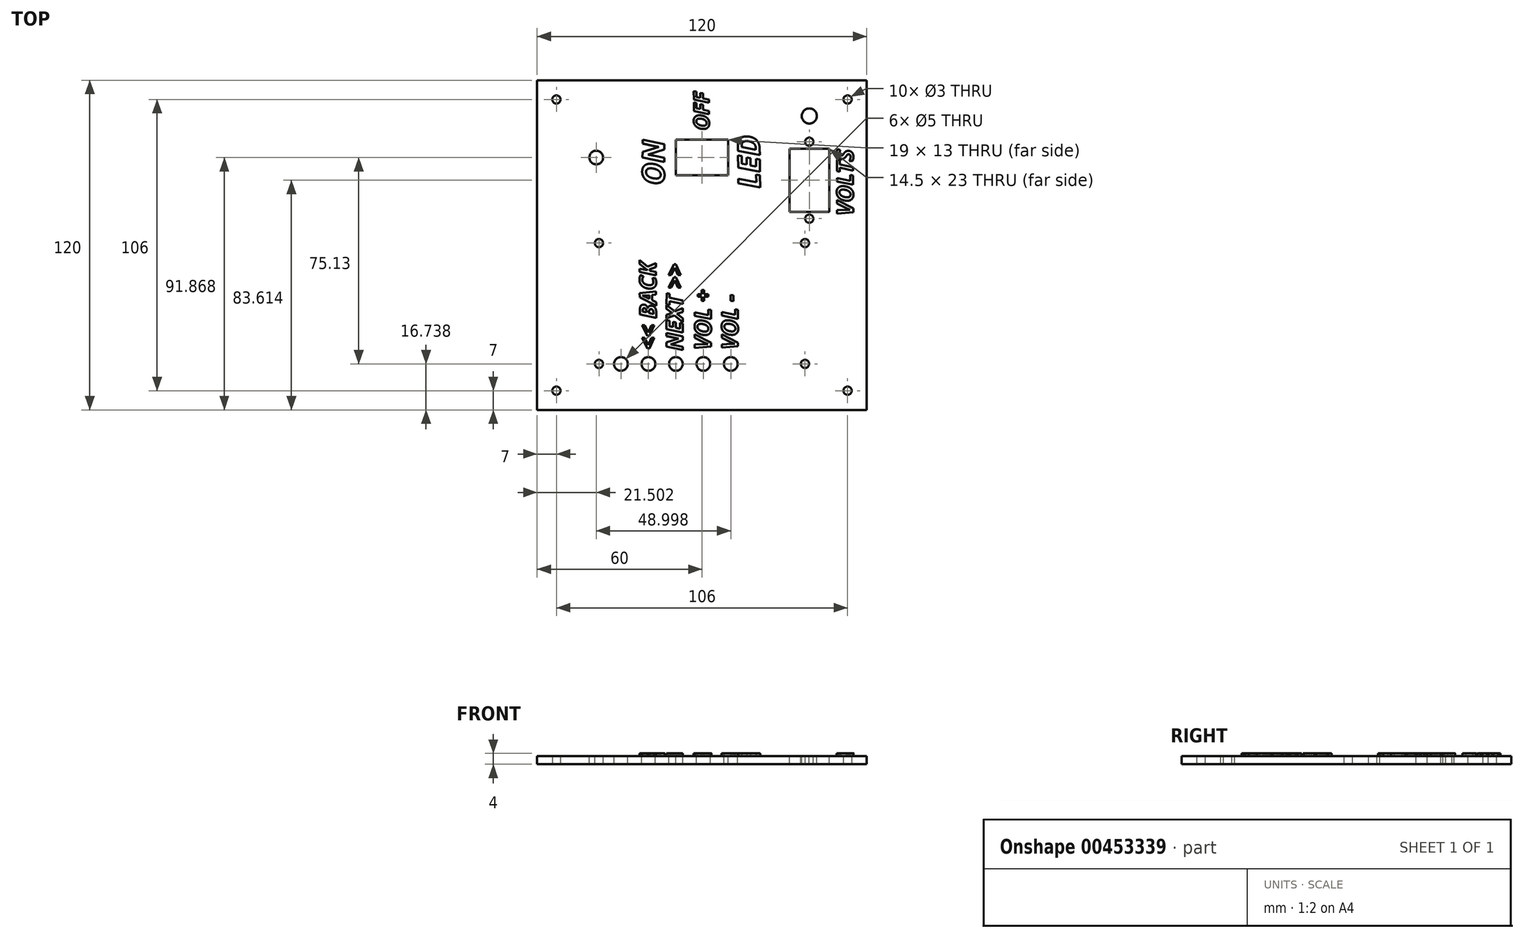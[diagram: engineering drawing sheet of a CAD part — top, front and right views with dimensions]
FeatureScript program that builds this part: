
annotation { "Feature Type Name" : "Feature", "Feature Type Description" : "" }
export const myFeature = defineFeature(function(context is Context, id is Id, definition is map)
    precondition{}
    {
        {
            var Q0;
            Q0=qCreatedBy(makeId("Top.planeOp"),FACE);
            var sketch = newSketch(context, id + "F0", { "sketchPlane" : qUnion([Q0])});
            skLineSegment(sketch, "E0.bottom", {"start": v(60, 60) * mm, "end": v(-60, 60) * mm});
            skLineSegment(sketch, "E0.top", {"start": v(60, -60) * mm, "end": v(-60, -60) * mm});
            skLineSegment(sketch, "E0.left", {"start": v(60, 60) * mm, "end": v(60, -60) * mm});
            skLineSegment(sketch, "E0.right", {"start": v(-60, 60) * mm, "end": v(-60, -60) * mm});
            skPoint(sketch, "E0.middle", {"position": v(0, 0) * mm});
            skLineSegment(sketch, "E1.0", {"start": v(-53, 53) * mm, "end": v(-53, -53) * mm, "construction": true});
            skLineSegment(sketch, "E1.1", {"start": v(53, 53) * mm, "end": v(-53, 53) * mm, "construction": true});
            skLineSegment(sketch, "E1.2", {"start": v(53, 53) * mm, "end": v(53, -53) * mm, "construction": true});
            skLineSegment(sketch, "E1.3", {"start": v(53, -53) * mm, "end": v(-53, -53) * mm, "construction": true});
            skCircle(sketch, "E2", {"center": v(-53, -53) * mm, "radius": 1.5 * mm});
            skCircle(sketch, "E3", {"center": v(-53, 53) * mm, "radius": 1.5 * mm});
            skCircle(sketch, "E4", {"center": v(53, 53) * mm, "radius": 1.5 * mm});
            skCircle(sketch, "E5", {"center": v(53, -53) * mm, "radius": 1.5 * mm});
            skSolve(sketch);
        }
        {
            var Q0;
            Q0 = qSketchRegion(id + "F0", true);
            extrude(context, id + "F1", {"entities" : qUnion([Q0]), "depth" : 3 * mm});
        }
        {
            var Q0;
            Q0=makeQuery(id+"F1.opExtrude","CAP_FACE",FACE,{"disambiguationData":[OSD([sQuery(id+"F0.wireOp",EDGE,"E0.bottom"),sQuery(id+"F0.wireOp",EDGE,"E0.top"),sQuery(id+"F0.wireOp",EDGE,"E0.left"),sQuery(id+"F0.wireOp",EDGE,"E0.right")])],"isStart":false});
            var sketch = newSketch(context, id + "F2", { "sketchPlane" : qUnion([Q0])});
            skLineSegment(sketch, "E6.bottom", {"start": v(37.5, 0.74) * mm, "end": v(-37.5, 0.74) * mm, "construction": true});
            skLineSegment(sketch, "E6.top", {"start": v(37.5, -43.26) * mm, "end": v(-37.5, -43.26) * mm, "construction": true});
            skLineSegment(sketch, "E6.left", {"start": v(37.5, 0.74) * mm, "end": v(37.5, -43.26) * mm, "construction": true});
            skLineSegment(sketch, "E6.right", {"start": v(-37.5, 0.74) * mm, "end": v(-37.5, -43.26) * mm, "construction": true});
            skPoint(sketch, "E6.middle", {"position": v(0, -21.26) * mm});
            skCircle(sketch, "E7", {"center": v(-37.5, 0.74) * mm, "radius": 1.5 * mm});
            skCircle(sketch, "E8", {"center": v(37.5, 0.74) * mm, "radius": 1.5 * mm});
            skCircle(sketch, "E9", {"center": v(37.5, -43.26) * mm, "radius": 1.5 * mm});
            skCircle(sketch, "E10", {"center": v(-37.5, -43.26) * mm, "radius": 1.5 * mm});
            skCircle(sketch, "E11", {"center": v(-29.5, -43.26) * mm, "radius": 2.5 * mm});
            skCircle(sketch, "E12", {"center": v(-19.5, -43.26) * mm, "radius": 2.5 * mm});
            skCircle(sketch, "E13", {"center": v(-9.5, -43.26) * mm, "radius": 2.5 * mm});
            skCircle(sketch, "E14", {"center": v(0.5, -43.26) * mm, "radius": 2.5 * mm});
            skCircle(sketch, "E15", {"center": v(10.5, -43.26) * mm, "radius": 2.5 * mm});
            skLineSegment(sketch, "E16.bottom", {"start": v(9.5, 38.37) * mm, "end": v(-9.5, 38.37) * mm});
            skLineSegment(sketch, "E16.top", {"start": v(9.5, 25.37) * mm, "end": v(-9.5, 25.37) * mm});
            skLineSegment(sketch, "E16.left", {"start": v(9.5, 38.37) * mm, "end": v(9.5, 25.37) * mm});
            skLineSegment(sketch, "E16.right", {"start": v(-9.5, 38.37) * mm, "end": v(-9.5, 25.37) * mm});
            skPoint(sketch, "E16.middle", {"position": v(0, 31.87) * mm});
            skSolve(sketch);
        }
        {
            var Q0;
            Q0=makeQuery(id+"F2.imprint","IMPRINT",FACE,{"disambiguationData":[TD([[makeQuery(id+"F2.imprint","IMPRINT",EDGE,{"derivedFrom":sQuery(id+"F2.wireOp",EDGE,"E7")}),-1.0]])]});
            var sketch = newSketch(context, id + "F3", { "sketchPlane" : qUnion([Q0])});
            skText(sketch, "E17", { "text": "PLAY", "fontName": "OpenSans-BoldItalic.ttf"});
            const initialGuessF3  = {"E17": [-0.02621, -0.03806, -0.00037, 1, 0.006]};
            skSetInitialGuess(sketch, initialGuessF3);
            skSolve(sketch);
        }
        {
            var Q0;
            Q0 = qConstructionFilter(qBodyType(qCreatedBy(id + "F3" ,EDGE), BodyType.WIRE), ConstructionObject.NO);
            extrude(context, id + "F4", {"bodyType" : ToolBodyType.SURFACE, "surfaceEntities" : qUnion([Q0]), "depth" : 1 * mm});
        }
        {
            var Q0;
            Q0=makeQuery(id+"F2.imprint","IMPRINT",FACE,{"disambiguationData":[TD([[makeQuery(id+"F2.imprint","IMPRINT",EDGE,{"derivedFrom":sQuery(id+"F2.wireOp",EDGE,"E7")}),-1.0]])]});
            var sketch = newSketch(context, id + "F5", { "sketchPlane" : qUnion([Q0])});
            skText(sketch, "E18", { "text": "<< BACK", "fontName": "OpenSans-BoldItalic.ttf"});
            const initialGuessF5  = {"E18": [-0.01657, -0.03808, -0.00626, 0.99998, 0.006]};
            skSetInitialGuess(sketch, initialGuessF5);
            skSolve(sketch);
        }
        {
            var Q0;
            Q0 = qSketchRegion(id + "F5", true);
            extrude(context, id + "F6", {"entities" : qUnion([Q0]), "operationType" : NewBodyOperationType.ADD, "depth" : 1 * mm});
        }
        {
            var Q0;
            Q0=makeQuery(id+"F2.imprint","IMPRINT",FACE,{"disambiguationData":[TD([[makeQuery(id+"F2.imprint","IMPRINT",EDGE,{"derivedFrom":sQuery(id+"F2.wireOp",EDGE,"E7")}),-1.0]])]});
            var sketch = newSketch(context, id + "F7", { "sketchPlane" : qUnion([Q0])});
            skText(sketch, "E19", { "text": "NEXT >>", "fontName": "OpenSans-BoldItalic.ttf"});
            const initialGuessF7  = {"E19": [-0.00696, -0.03837, 0.00128, 1, 0.006]};
            skSetInitialGuess(sketch, initialGuessF7);
            skSolve(sketch);
        }
        {
            var Q0;
            Q0 = qSketchRegion(id + "F7", true);
            extrude(context, id + "F8", {"entities" : qUnion([Q0]), "operationType" : NewBodyOperationType.ADD, "depth" : 1 * mm});
        }
        {
            var Q0;
            Q0=makeQuery(id+"F2.imprint","IMPRINT",FACE,{"disambiguationData":[TD([[makeQuery(id+"F2.imprint","IMPRINT",EDGE,{"derivedFrom":sQuery(id+"F2.wireOp",EDGE,"E7")}),-1.0]])]});
            var sketch = newSketch(context, id + "F9", { "sketchPlane" : qUnion([Q0])});
            skText(sketch, "E20", { "text": "VOL +", "fontName": "OpenSans-BoldItalic.ttf"});
            const initialGuessF9  = {"E20": [0.00332, -0.03817, -0.00012, 1, 0.006]};
            skSetInitialGuess(sketch, initialGuessF9);
            skSolve(sketch);
        }
        {
            var Q0;
            Q0 = qSketchRegion(id + "F9", true);
            extrude(context, id + "F10", {"entities" : qUnion([Q0]), "operationType" : NewBodyOperationType.ADD, "depth" : 1 * mm});
        }
        {
            var Q0;
            Q0=makeQuery(id+"F2.imprint","IMPRINT",FACE,{"disambiguationData":[TD([[makeQuery(id+"F2.imprint","IMPRINT",EDGE,{"derivedFrom":sQuery(id+"F2.wireOp",EDGE,"E7")}),-1.0]])]});
            var sketch = newSketch(context, id + "F11", { "sketchPlane" : qUnion([Q0])});
            skText(sketch, "E21", { "text": "VOL -", "fontName": "OpenSans-BoldItalic.ttf"});
            const initialGuessF11  = {"E21": [0.01313, -0.03811, 0.00122, 1, 0.006]};
            skSetInitialGuess(sketch, initialGuessF11);
            skSolve(sketch);
        }
        {
            var Q0;
            Q0 = qSketchRegion(id + "F11", true);
            extrude(context, id + "F12", {"entities" : qUnion([Q0]), "operationType" : NewBodyOperationType.ADD, "depth" : 1 * mm});
        }
        {
            var Q0;
            Q0 = qSketchRegion(id + "F0", true);
            extrude(context, id + "F13", {"entities" : qUnion([Q0]), "operationType" : NewBodyOperationType.REMOVE, "oppositeDirection" : true, "depth" : 4 * mm});
        }
        {
            var Q0;
            Q0 = qSketchRegion(id + "F2", true);
            extrude(context, id + "F14", {"entities" : qUnion([Q0]), "operationType" : NewBodyOperationType.REMOVE, "oppositeDirection" : true, "depth" : 3 * mm});
        }
        {
            var Q0;
            {var subQ92=sQuery(id+"F0.wireOp",EDGE,"E0.right");var subQ95=sQuery(id+"F0.wireOp",EDGE,"E3");var subQ98=sQuery(id+"F0.wireOp",EDGE,"E4");var subQ103=sQuery(id+"F0.wireOp",EDGE,"E0.left");var subQ105=sQuery(id+"F0.wireOp",EDGE,"E5");var subQ107=sQuery(id+"F0.wireOp",EDGE,"E0.top");var subQ110=sQuery(id+"F0.wireOp",EDGE,"E2");var subQ132=sQuery(id+"F0.wireOp",EDGE,"E0.bottom");var subQ133=makeQuery(id+"F1.opExtrude","SWEPT_FACE",FACE,{"disambiguationData":[OSD([subQ132])]});Q0=makeQuery(id+"F12.boolean.opBoolean","SPLIT",FACE,{"disambiguationData":[TD([subQ133])],"derivedFrom":makeQuery(id+"F10.boolean.opBoolean","SPLIT",FACE,{"disambiguationData":[TD([subQ133])],"derivedFrom":makeQuery(id+"F6.boolean.opBoolean","SPLIT",FACE,{"disambiguationData":[TD([subQ133])],"derivedFrom":makeQuery(id+"F1.opExtrude","CAP_FACE",FACE,{"disambiguationData":[OSD([subQ132,subQ107,subQ103,subQ92,subQ110,subQ95,subQ98,subQ105])],"isStart":false})})})});}
            var sketch = newSketch(context, id + "F15", { "sketchPlane" : qUnion([Q0])});
            skText(sketch, "E22", { "text": "ON", "fontName": "OpenSans-BoldItalic.ttf"});
            const initialGuessF15  = {"E22": [-0.01374, 0.02185, 0.0028, 1, 0.008]};
            skSetInitialGuess(sketch, initialGuessF15);
            skSolve(sketch);
        }
        {
            var Q0;
            Q0 = qSketchRegion(id + "F15", true);
            extrude(context, id + "F16", {"entities" : qUnion([Q0]), "operationType" : NewBodyOperationType.ADD, "depth" : 1 * mm});
        }
        {
            var Q0;
            {var subQ66=sQuery(id+"F0.wireOp",EDGE,"E0.bottom");var subQ67=makeQuery(id+"F1.opExtrude","SWEPT_FACE",FACE,{"disambiguationData":[OSD([subQ66])]});var subQ88=sQuery(id+"F0.wireOp",EDGE,"E2");var subQ90=sQuery(id+"F0.wireOp",EDGE,"E0.top");var subQ92=sQuery(id+"F0.wireOp",EDGE,"E5");var subQ94=sQuery(id+"F0.wireOp",EDGE,"E0.left");var subQ99=sQuery(id+"F0.wireOp",EDGE,"E4");var subQ102=sQuery(id+"F0.wireOp",EDGE,"E3");var subQ105=sQuery(id+"F0.wireOp",EDGE,"E0.right");Q0=makeQuery(id+"F16.boolean.opBoolean","SPLIT",FACE,{"disambiguationData":[TD([subQ67])],"derivedFrom":makeQuery(id+"F12.boolean.opBoolean","SPLIT",FACE,{"disambiguationData":[TD([subQ67])],"derivedFrom":makeQuery(id+"F10.boolean.opBoolean","SPLIT",FACE,{"disambiguationData":[TD([subQ67])],"derivedFrom":makeQuery(id+"F6.boolean.opBoolean","SPLIT",FACE,{"disambiguationData":[TD([subQ67])],"derivedFrom":makeQuery(id+"F1.opExtrude","CAP_FACE",FACE,{"disambiguationData":[OSD([subQ66,subQ90,subQ94,subQ105,subQ88,subQ102,subQ99,subQ92])],"isStart":false})})})})});}
            var sketch = newSketch(context, id + "F17", { "sketchPlane" : qUnion([Q0])});
            skText(sketch, "E23", { "text": "LED", "fontName": "OpenSans-BoldItalic.ttf"});
            const initialGuessF17  = {"E23": [0.02119, 0.02066, -0.01332, 0.99991, 0.008]};
            skSetInitialGuess(sketch, initialGuessF17);
            skSolve(sketch);
        }
        {
            var Q0;
            Q0 = qSketchRegion(id + "F17", true);
            extrude(context, id + "F18", {"entities" : qUnion([Q0]), "operationType" : NewBodyOperationType.ADD, "depth" : 1 * mm});
        }
        {
            var Q0;
            Q0 = qSketchRegion(id + "F2", true);
            extrude(context, id + "F19", {"entities" : qUnion([Q0]), "operationType" : NewBodyOperationType.REMOVE, "oppositeDirection" : true, "depth" : 5 * mm});
        }
        {
            var Q0;
            {var subQ78=sQuery(id+"F0.wireOp",EDGE,"E0.bottom");var subQ79=makeQuery(id+"F1.opExtrude","SWEPT_FACE",FACE,{"disambiguationData":[OSD([subQ78])]});var subQ100=sQuery(id+"F0.wireOp",EDGE,"E2");var subQ102=sQuery(id+"F0.wireOp",EDGE,"E0.top");var subQ104=sQuery(id+"F0.wireOp",EDGE,"E5");var subQ106=sQuery(id+"F0.wireOp",EDGE,"E0.left");var subQ111=sQuery(id+"F0.wireOp",EDGE,"E4");var subQ114=sQuery(id+"F0.wireOp",EDGE,"E3");var subQ117=sQuery(id+"F0.wireOp",EDGE,"E0.right");Q0=makeQuery(id+"F18.boolean.opBoolean","SPLIT",FACE,{"disambiguationData":[TD([subQ79])],"derivedFrom":makeQuery(id+"F16.boolean.opBoolean","SPLIT",FACE,{"disambiguationData":[TD([subQ79])],"derivedFrom":makeQuery(id+"F12.boolean.opBoolean","SPLIT",FACE,{"disambiguationData":[TD([subQ79])],"derivedFrom":makeQuery(id+"F10.boolean.opBoolean","SPLIT",FACE,{"disambiguationData":[TD([subQ79])],"derivedFrom":makeQuery(id+"F6.boolean.opBoolean","SPLIT",FACE,{"disambiguationData":[TD([subQ79])],"derivedFrom":makeQuery(id+"F1.opExtrude","CAP_FACE",FACE,{"disambiguationData":[OSD([subQ78,subQ102,subQ106,subQ117,subQ100,subQ114,subQ111,subQ104])],"isStart":false})})})})})});}
            var sketch = newSketch(context, id + "F20", { "sketchPlane" : qUnion([Q0])});
            skText(sketch, "E24", { "text": "OFF", "fontName": "OpenSans-BoldItalic.ttf"});
            const initialGuessF20  = {"E24": [0.0026, 0.0418, -0.00228, 1, 0.0056]};
            skSetInitialGuess(sketch, initialGuessF20);
            skSolve(sketch);
        }
        {
            var Q0;
            Q0 = qSketchRegion(id + "F20", true);
            extrude(context, id + "F21", {"entities" : qUnion([Q0]), "operationType" : NewBodyOperationType.ADD, "depth" : 1 * mm});
        }
        {
            var Q0;
            {var subQ83=sQuery(id+"F0.wireOp",EDGE,"E0.bottom");var subQ84=makeQuery(id+"F1.opExtrude","SWEPT_FACE",FACE,{"disambiguationData":[OSD([subQ83])]});var subQ105=sQuery(id+"F0.wireOp",EDGE,"E2");var subQ107=sQuery(id+"F0.wireOp",EDGE,"E0.top");var subQ109=sQuery(id+"F0.wireOp",EDGE,"E5");var subQ111=sQuery(id+"F0.wireOp",EDGE,"E0.left");var subQ116=sQuery(id+"F0.wireOp",EDGE,"E4");var subQ119=sQuery(id+"F0.wireOp",EDGE,"E3");var subQ122=sQuery(id+"F0.wireOp",EDGE,"E0.right");Q0=makeQuery(id+"F21.boolean.opBoolean","SPLIT",FACE,{"disambiguationData":[TD([subQ84])],"derivedFrom":makeQuery(id+"F18.boolean.opBoolean","SPLIT",FACE,{"disambiguationData":[TD([subQ84])],"derivedFrom":makeQuery(id+"F16.boolean.opBoolean","SPLIT",FACE,{"disambiguationData":[TD([subQ84])],"derivedFrom":makeQuery(id+"F12.boolean.opBoolean","SPLIT",FACE,{"disambiguationData":[TD([subQ84])],"derivedFrom":makeQuery(id+"F10.boolean.opBoolean","SPLIT",FACE,{"disambiguationData":[TD([subQ84])],"derivedFrom":makeQuery(id+"F6.boolean.opBoolean","SPLIT",FACE,{"disambiguationData":[TD([subQ84])],"derivedFrom":makeQuery(id+"F1.opExtrude","CAP_FACE",FACE,{"disambiguationData":[OSD([subQ83,subQ107,subQ111,subQ122,subQ105,subQ119,subQ116,subQ109])],"isStart":false})})})})})})});}
            var sketch = newSketch(context, id + "F22", { "sketchPlane" : qUnion([Q0])});
            skLineSegment(sketch, "E25.bottom", {"start": v(46.32, 35.11) * mm, "end": v(31.82, 35.11) * mm});
            skLineSegment(sketch, "E25.top", {"start": v(46.32, 12.11) * mm, "end": v(31.82, 12.11) * mm});
            skLineSegment(sketch, "E25.left", {"start": v(46.32, 35.11) * mm, "end": v(46.32, 12.11) * mm});
            skLineSegment(sketch, "E25.right", {"start": v(31.82, 35.11) * mm, "end": v(31.82, 12.11) * mm});
            skPoint(sketch, "E25.middle", {"position": v(39.07, 23.61) * mm});
            skLineSegment(sketch, "E26", {"start": v(39.07, 23.61) * mm, "end": v(39.07, 43.43) * mm, "construction": true});
            skPoint(sketch, "E26.endSnap0", {"position": v(39.07, 35.11) * mm});
            skLineSegment(sketch, "E27", {"start": v(39.07, 43.43) * mm, "end": v(39.07, 9.61) * mm, "construction": true});
            skCircle(sketch, "E28", {"center": v(39.07, 9.61) * mm, "radius": 1.5 * mm});
            skLineSegment(sketch, "E29", {"start": v(39.07, 23.61) * mm, "end": v(28.39, 23.47) * mm, "construction": true});
            skCircle(sketch, "E30", {"center": v(39.07, 37.61) * mm, "radius": 1.5 * mm});
            skCircle(sketch, "E31", {"center": v(39.07, 47) * mm, "radius": 2.75 * mm});
            skSolve(sketch);
        }
        {
            var Q0;
            Q0 = qSketchRegion(id + "F22", true);
            extrude(context, id + "F23", {"entities" : qUnion([Q0]), "operationType" : NewBodyOperationType.REMOVE, "oppositeDirection" : true, "depth" : 5 * mm});
        }
        {
            var Q0;
            {var subQ60=sQuery(id+"F0.wireOp",EDGE,"E0.bottom");var subQ61=makeQuery(id+"F1.opExtrude","SWEPT_FACE",FACE,{"disambiguationData":[OSD([subQ60])]});var subQ85=sQuery(id+"F0.wireOp",EDGE,"E2");var subQ89=sQuery(id+"F0.wireOp",EDGE,"E0.top");var subQ92=sQuery(id+"F0.wireOp",EDGE,"E5");var subQ95=sQuery(id+"F0.wireOp",EDGE,"E0.left");var subQ98=sQuery(id+"F0.wireOp",EDGE,"E4");var subQ101=sQuery(id+"F0.wireOp",EDGE,"E3");var subQ105=sQuery(id+"F0.wireOp",EDGE,"E0.right");Q0=makeQuery(id+"F21.boolean.opBoolean","SPLIT",FACE,{"disambiguationData":[TD([subQ61])],"derivedFrom":makeQuery(id+"F18.boolean.opBoolean","SPLIT",FACE,{"disambiguationData":[TD([subQ61])],"derivedFrom":makeQuery(id+"F16.boolean.opBoolean","SPLIT",FACE,{"disambiguationData":[TD([subQ61])],"derivedFrom":makeQuery(id+"F12.boolean.opBoolean","SPLIT",FACE,{"disambiguationData":[TD([subQ61])],"derivedFrom":makeQuery(id+"F10.boolean.opBoolean","SPLIT",FACE,{"disambiguationData":[TD([subQ61])],"derivedFrom":makeQuery(id+"F6.boolean.opBoolean","SPLIT",FACE,{"disambiguationData":[TD([subQ61])],"derivedFrom":makeQuery(id+"F1.opExtrude","CAP_FACE",FACE,{"disambiguationData":[OSD([subQ60,subQ89,subQ95,subQ105,subQ85,subQ101,subQ98,subQ92])],"isStart":false})})})})})})});}
            var sketch = newSketch(context, id + "F24", { "sketchPlane" : qUnion([Q0])});
            skText(sketch, "E32", { "text": "VOLTS", "fontName": "OpenSans-BoldItalic.ttf"});
            const initialGuessF24  = {"E32": [0.05507, 0.01073, -0.00147, 1, 0.006]};
            skSetInitialGuess(sketch, initialGuessF24);
            skSolve(sketch);
        }
        {
            var Q0;
            Q0 = qSketchRegion(id + "F24", true);
            extrude(context, id + "F25", {"entities" : qUnion([Q0]), "operationType" : NewBodyOperationType.ADD, "depth" : 1 * mm});
        }
        {
            var Q0;
            {var subQ60=sQuery(id+"F0.wireOp",EDGE,"E0.bottom");var subQ61=makeQuery(id+"F1.opExtrude","SWEPT_FACE",FACE,{"disambiguationData":[OSD([subQ60])]});var subQ87=sQuery(id+"F0.wireOp",EDGE,"E2");var subQ91=sQuery(id+"F0.wireOp",EDGE,"E0.top");var subQ94=sQuery(id+"F0.wireOp",EDGE,"E5");var subQ97=sQuery(id+"F0.wireOp",EDGE,"E0.left");var subQ100=sQuery(id+"F0.wireOp",EDGE,"E4");var subQ103=sQuery(id+"F0.wireOp",EDGE,"E3");var subQ107=sQuery(id+"F0.wireOp",EDGE,"E0.right");Q0=makeQuery(id+"F25.boolean.opBoolean","SPLIT",FACE,{"disambiguationData":[TD([subQ61])],"derivedFrom":makeQuery(id+"F21.boolean.opBoolean","SPLIT",FACE,{"disambiguationData":[TD([subQ61])],"derivedFrom":makeQuery(id+"F18.boolean.opBoolean","SPLIT",FACE,{"disambiguationData":[TD([subQ61])],"derivedFrom":makeQuery(id+"F16.boolean.opBoolean","SPLIT",FACE,{"disambiguationData":[TD([subQ61])],"derivedFrom":makeQuery(id+"F12.boolean.opBoolean","SPLIT",FACE,{"disambiguationData":[TD([subQ61])],"derivedFrom":makeQuery(id+"F10.boolean.opBoolean","SPLIT",FACE,{"disambiguationData":[TD([subQ61])],"derivedFrom":makeQuery(id+"F6.boolean.opBoolean","SPLIT",FACE,{"disambiguationData":[TD([subQ61])],"derivedFrom":makeQuery(id+"F1.opExtrude","CAP_FACE",FACE,{"disambiguationData":[OSD([subQ60,subQ91,subQ97,subQ107,subQ87,subQ103,subQ100,subQ94])],"isStart":false})})})})})})})});}
            var sketch = newSketch(context, id + "F26", { "sketchPlane" : qUnion([Q0])});
            skLineSegment(sketch, "E33", {"start": v(-9.5, 31.87) * mm, "end": v(-52.74, 31.87) * mm, "construction": true});
            skCircle(sketch, "E34", {"center": v(-38.5, 31.87) * mm, "radius": 2.5 * mm});
            skSolve(sketch);
        }
        {
            var Q0;
            Q0 = qSketchRegion(id + "F26", true);
            extrude(context, id + "F27", {"entities" : qUnion([Q0]), "operationType" : NewBodyOperationType.REMOVE, "oppositeDirection" : true, "depth" : 5 * mm});
        }
    });
